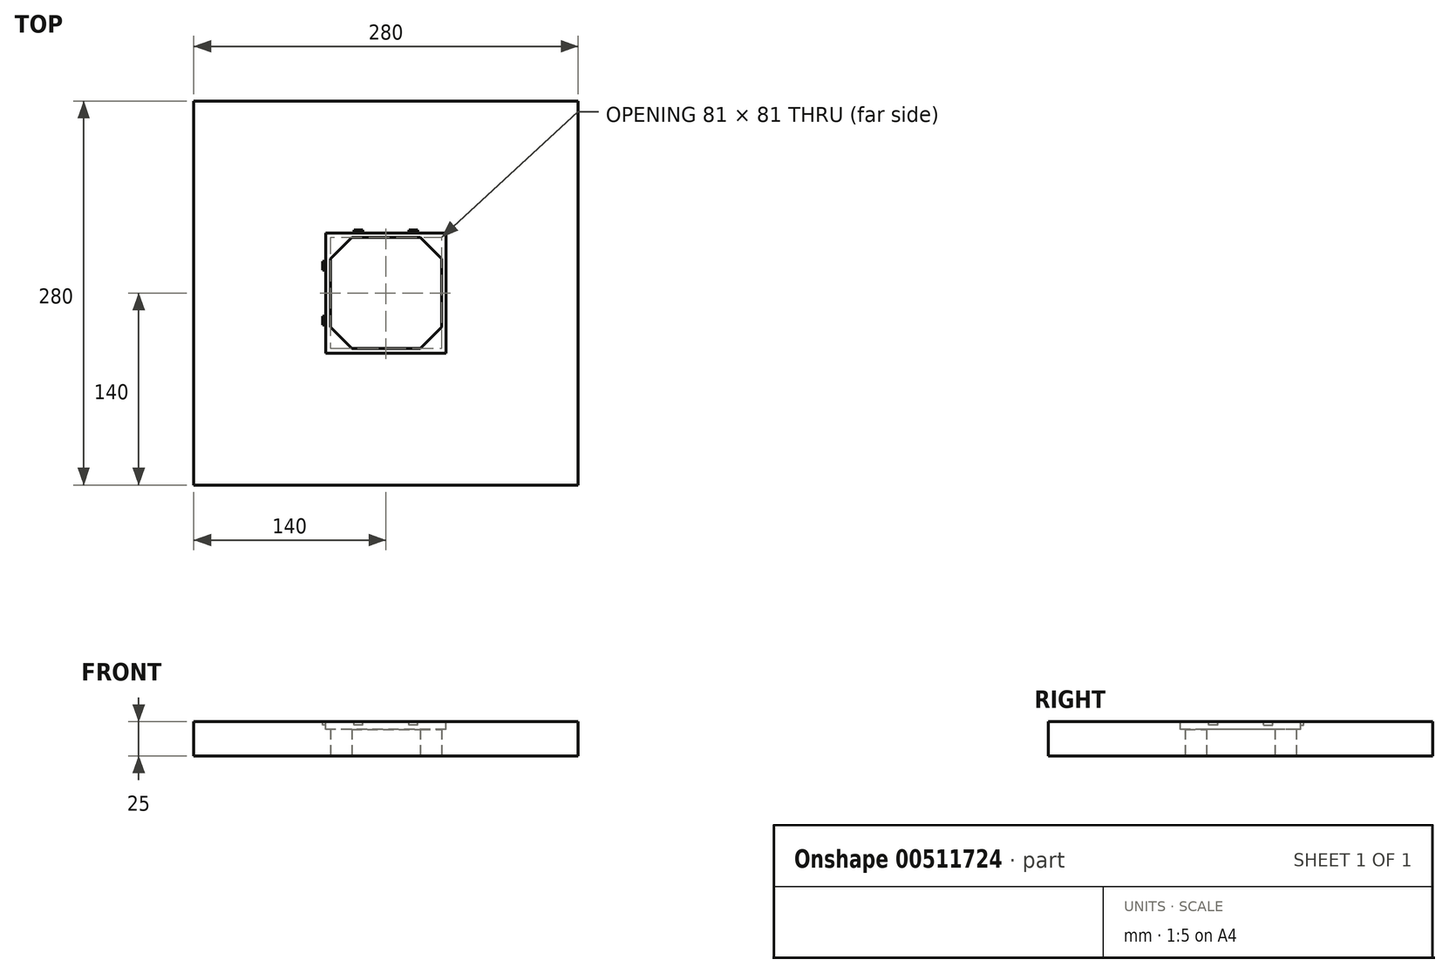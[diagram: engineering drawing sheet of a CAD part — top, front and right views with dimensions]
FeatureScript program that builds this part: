
annotation { "Feature Type Name" : "Feature", "Feature Type Description" : "" }
export const myFeature = defineFeature(function(context is Context, id is Id, definition is map)
    precondition{}
    {
        {
            var Q0;
            Q0=qCreatedBy(makeId("Top.planeOp"),FACE);
            var sketch = newSketch(context, id + "F0", { "sketchPlane" : qUnion([Q0])});
            skLineSegment(sketch, "E0.bottom", {"start": v(-24.94, 40.5) * mm, "end": v(24.94, 40.5) * mm});
            skLineSegment(sketch, "E0.top", {"start": v(-24.94, -40.5) * mm, "end": v(24.94, -40.5) * mm});
            skLineSegment(sketch, "E0.left", {"start": v(-40.5, 24.94) * mm, "end": v(-40.5, -24.94) * mm});
            skLineSegment(sketch, "E0.right", {"start": v(40.5, 24.94) * mm, "end": v(40.5, -24.94) * mm});
            skPoint(sketch, "E0.middle", {"position": v(0, 0) * mm});
            skLineSegment(sketch, "E1", {"start": v(24.94, -40.5) * mm, "end": v(40.5, -24.94) * mm});
            skLineSegment(sketch, "E2", {"start": v(-24.94, 40.5) * mm, "end": v(-40.5, 24.94) * mm});
            skLineSegment(sketch, "E3", {"start": v(-24.94, -40.5) * mm, "end": v(-40.5, -24.94) * mm});
            skLineSegment(sketch, "E4", {"start": v(24.94, 40.5) * mm, "end": v(40.5, 24.94) * mm});
            skPoint(sketch, "E5.orphan", {"position": v(40.5, 40.5) * mm});
            skPoint(sketch, "E6.orphan", {"position": v(40.5, -40.5) * mm});
            skPoint(sketch, "E7.orphan", {"position": v(-40.5, -40.5) * mm});
            skPoint(sketch, "E8.orphan", {"position": v(-40.5, 40.5) * mm});
            skLineSegment(sketch, "E9.bottom", {"start": v(140, 140) * mm, "end": v(-140, 140) * mm});
            skLineSegment(sketch, "E9.top", {"start": v(140, -140) * mm, "end": v(-140, -140) * mm});
            skLineSegment(sketch, "E9.left", {"start": v(140, 140) * mm, "end": v(140, -140) * mm});
            skLineSegment(sketch, "E9.right", {"start": v(-140, 140) * mm, "end": v(-140, -140) * mm});
            skSolve(sketch);
        }
        {
            var Q0;
            Q0 = qSketchRegion(id + "F0", true);
            extrude(context, id + "F1", {"entities" : qUnion([Q0]), "depth" : 25 * mm});
        }
        {
            var Q0;
            Q0=makeQuery(id+"F1.opExtrude","CAP_FACE",FACE,{"disambiguationData":[OSD([sQuery(id+"F0.wireOp",EDGE,"E0.bottom"),sQuery(id+"F0.wireOp",EDGE,"E0.top"),sQuery(id+"F0.wireOp",EDGE,"E0.left"),sQuery(id+"F0.wireOp",EDGE,"E0.right"),sQuery(id+"F0.wireOp",EDGE,"E1"),sQuery(id+"F0.wireOp",EDGE,"E2"),sQuery(id+"F0.wireOp",EDGE,"E3"),sQuery(id+"F0.wireOp",EDGE,"E4"),sQuery(id+"F0.wireOp",EDGE,"E9.bottom"),sQuery(id+"F0.wireOp",EDGE,"E9.top"),sQuery(id+"F0.wireOp",EDGE,"E9.left"),sQuery(id+"F0.wireOp",EDGE,"E9.right")])],"isStart":false});
            var sketch = newSketch(context, id + "F2", { "sketchPlane" : qUnion([Q0])});
            skLineSegment(sketch, "E10", {"start": v(-1, 0) * mm, "end": v(-68.17, 0) * mm, "construction": true});
            skLineSegment(sketch, "E11.0", {"start": v(-0.52, 20) * mm, "end": v(-67.68, 20) * mm, "construction": true});
            skLineSegment(sketch, "E12.0", {"start": v(-24.94, 40.5) * mm, "end": v(24.94, 40.5) * mm});
            skLineSegment(sketch, "E13.0", {"start": v(-1, -20) * mm, "end": v(-68.17, -20) * mm, "construction": true});
            skPoint(sketch, "E14.center", {"position": v(0, 0) * mm});
            skLineSegment(sketch, "E15.bottom", {"start": v(-35, 16.75) * mm, "end": v(-35, 23.25) * mm});
            skLineSegment(sketch, "E15.top", {"start": v(-46, 16.75) * mm, "end": v(-46, 23.25) * mm});
            skLineSegment(sketch, "E15.left", {"start": v(-35, 16.75) * mm, "end": v(-46, 16.75) * mm});
            skLineSegment(sketch, "E15.right", {"start": v(-35, 23.25) * mm, "end": v(-46, 23.25) * mm});
            skPoint(sketch, "E15.middle", {"position": v(-40.5, 20) * mm});
            skLineSegment(sketch, "E16.MirrorCS", {"start": v(-35, -16.75) * mm, "end": v(-35, -23.25) * mm});
            skLineSegment(sketch, "E17.MirrorCS", {"start": v(-35, -16.75) * mm, "end": v(-46, -16.75) * mm});
            skLineSegment(sketch, "E18.MirrorCS", {"start": v(-46, -16.75) * mm, "end": v(-46, -23.25) * mm});
            skLineSegment(sketch, "E19.MirrorCS", {"start": v(-35, -23.25) * mm, "end": v(-46, -23.25) * mm});
            skLineSegment(sketch, "E20.1.0", {"start": v(16.75, 35) * mm, "end": v(16.75, 46) * mm});
            skLineSegment(sketch, "E20.1.1", {"start": v(16.75, 35) * mm, "end": v(23.25, 35) * mm});
            skLineSegment(sketch, "E20.1.2", {"start": v(23.25, 35) * mm, "end": v(23.25, 46) * mm});
            skLineSegment(sketch, "E20.1.3", {"start": v(16.75, 46) * mm, "end": v(23.25, 46) * mm});
            skLineSegment(sketch, "E20.1.4", {"start": v(-16.75, 35) * mm, "end": v(-16.75, 46) * mm});
            skLineSegment(sketch, "E20.1.5", {"start": v(-16.75, 35) * mm, "end": v(-23.25, 35) * mm});
            skLineSegment(sketch, "E20.1.6", {"start": v(-23.25, 35) * mm, "end": v(-23.25, 46) * mm});
            skLineSegment(sketch, "E20.1.7", {"start": v(-16.75, 46) * mm, "end": v(-23.25, 46) * mm});
            skLineSegment(sketch, "E20.anchor1", {"start": v(0, 0) * mm, "end": v(-46, 16.75) * mm, "construction": true});
            skLineSegment(sketch, "E20.anchor2", {"start": v(0, 0) * mm, "end": v(16.75, 46) * mm, "construction": true});
            skSolve(sketch);
        }
        {
            var Q0;
            Q0 = qSketchRegion(id + "F2", true);
            extrude(context, id + "F3", {"entities" : qUnion([Q0]), "operationType" : NewBodyOperationType.REMOVE, "depth" : -2.5 * mm});
        }
        {
            var Q0;
            Q0=makeQuery(id+"F1.opExtrude","CAP_FACE",FACE,{"disambiguationData":[OSD([sQuery(id+"F0.wireOp",EDGE,"E0.bottom"),sQuery(id+"F0.wireOp",EDGE,"E0.top"),sQuery(id+"F0.wireOp",EDGE,"E0.left"),sQuery(id+"F0.wireOp",EDGE,"E0.right"),sQuery(id+"F0.wireOp",EDGE,"E1"),sQuery(id+"F0.wireOp",EDGE,"E2"),sQuery(id+"F0.wireOp",EDGE,"E3"),sQuery(id+"F0.wireOp",EDGE,"E4"),sQuery(id+"F0.wireOp",EDGE,"E9.bottom"),sQuery(id+"F0.wireOp",EDGE,"E9.top"),sQuery(id+"F0.wireOp",EDGE,"E9.left"),sQuery(id+"F0.wireOp",EDGE,"E9.right")])],"isStart":false});
            var sketch = newSketch(context, id + "F4", { "sketchPlane" : qUnion([Q0])});
            skLineSegment(sketch, "E21.bottom", {"start": v(43.8, 43.8) * mm, "end": v(-43.8, 43.8) * mm});
            skLineSegment(sketch, "E21.top", {"start": v(43.8, -43.8) * mm, "end": v(-43.8, -43.8) * mm});
            skLineSegment(sketch, "E21.left", {"start": v(43.8, 43.8) * mm, "end": v(43.8, -43.8) * mm});
            skLineSegment(sketch, "E21.right", {"start": v(-43.8, 43.8) * mm, "end": v(-43.8, -43.8) * mm});
            skPoint(sketch, "E21.middle", {"position": v(0, 0) * mm});
            skSolve(sketch);
        }
        {
            var Q0;
            Q0 = qSketchRegion(id + "F4", true);
            extrude(context, id + "F5", {"entities" : qUnion([Q0]), "operationType" : NewBodyOperationType.REMOVE, "oppositeDirection" : true, "depth" : 5.6 * mm, "offsetDistance" : 25 * mm});
        }
    });
